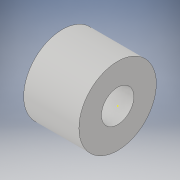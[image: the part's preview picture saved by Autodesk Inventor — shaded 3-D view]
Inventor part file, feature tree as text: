
AUTODESK INVENTOR PART (.ipt)
format: ipt  version: 2019 (Build 230136000, 136)  size: 97,280 bytes
history: native  units: mm
features: sketch x2, extrude x1
ambient origin geometry x8: Origin, YZ Plane, XZ Plane, XY Plane, X Axis, Y Axis, Z Axis, Center Point
bodies: Solid1 (feature_tree)
feature tree (3):
  extrude  "Extrusion1"  Depth=25.0mm TaperAngle=0.0deg
  sketch  "Sketch2"
  sketch  "Sketch1"  dims[d0=35.0mm d1=25.0mm d2=0.0mm]
